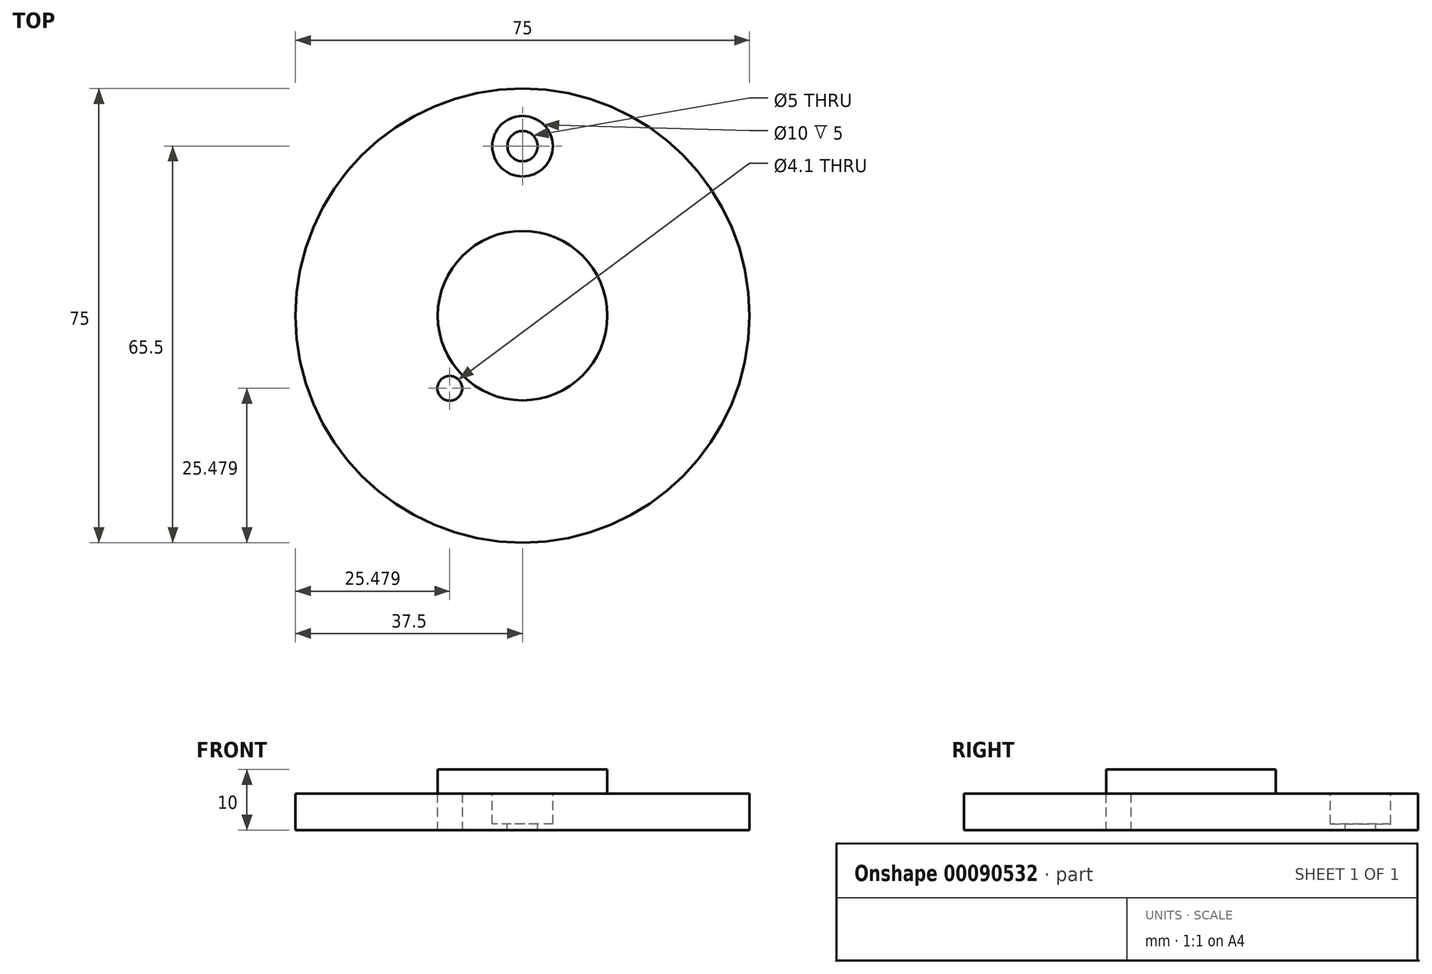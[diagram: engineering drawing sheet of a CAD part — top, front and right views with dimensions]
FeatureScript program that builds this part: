
annotation { "Feature Type Name" : "Feature", "Feature Type Description" : "" }
export const myFeature = defineFeature(function(context is Context, id is Id, definition is map)
    precondition{}
    {
        {
            var Q0;
            Q0=qCreatedBy(makeId("Top.planeOp"),FACE);
            var sketch = newSketch(context, id + "F0", { "sketchPlane" : qUnion([Q0])});
            skCircle(sketch, "E0", {"center": v(0, 0) * mm, "radius": 37.5 * mm});
            skSolve(sketch);
        }
        {
            var Q0;
            Q0=makeQuery(id+"F0.imprint","IMPRINT",FACE,{"disambiguationData":[TD([[makeQuery(id+"F0.imprint","IMPRINT",EDGE,{"derivedFrom":sQuery(id+"F0.wireOp",EDGE,"E0")}),1.0]])]});
            extrude(context, id + "F1", {"entities" : qUnion([Q0]), "depth" : 10 * mm});
        }
        {
            var Q0;
            Q0=makeQuery(id+"F1.opExtrude","CAP_FACE",FACE,{"disambiguationData":[OSD([sQuery(id+"F0.wireOp",EDGE,"E0")])],"isStart":false});
            var sketch = newSketch(context, id + "F2", { "sketchPlane" : qUnion([Q0])});
            skCircle(sketch, "E1", {"center": v(0, 0) * mm, "radius": 14 * mm});
            skSolve(sketch);
        }
        {
            var Q0;
            Q0=makeQuery(id+"F2.imprint","IMPRINT",FACE,{"disambiguationData":[TD([[makeQuery(id+"F2.imprint","IMPRINT",EDGE,{"derivedFrom":sQuery(id+"F2.wireOp",EDGE,"E1")}),-1.0]])]});
            extrude(context, id + "F3", {"entities" : qUnion([Q0]), "operationType" : NewBodyOperationType.REMOVE, "oppositeDirection" : true, "depth" : 4 * mm});
        }
        {
            var Q0;
            Q0=makeQuery(id+"F3.boolean.opBoolean","COPY",FACE,{"derivedFrom":makeQuery(id+"F3.opExtrude","CAP_FACE",FACE,{"disambiguationData":[OSD([sQuery(id+"F0.wireOp",EDGE,"E0"),sQuery(id+"F2.wireOp",EDGE,"E1")])],"isStart":false})});
            var sketch = newSketch(context, id + "F4", { "sketchPlane" : qUnion([Q0])});
            skCircle(sketch, "E2", {"center": v(0, 0) * mm, "radius": 28 * mm, "construction": true});
            skPoint(sketch, "E3", {"position": v(0, 28) * mm});
            skSolve(sketch);
        }
        {
            var Q0;
            Q0=sQuery(id+"F4.wireOp",VERTEX,"E3");
            var Q1;
            Q1=sQuery(id+"F4.wireOp",VERTEX,"5a48b65d-17f8-4e40-85f7-70837d0b4d29.1.0");
            var Q2;
            Q2=sQuery(id+"F4.wireOp",VERTEX,"5a48b65d-17f8-4e40-85f7-70837d0b4d29.2.0");
            var Q3;
            Q3=sQuery(id+"F4.wireOp",VERTEX,"5a48b65d-17f8-4e40-85f7-70837d0b4d29.3.0");
            var Q4;
            Q4=makeQuery(id+"F1.opExtrude","SWEPT_BODY",BODY,{"disambiguationData":[OSD([sQuery(id+"F0.wireOp",EDGE,"E0")])]});
            hole(context, id + "F5", {"style" : HoleStyle.C_BORE, "endStyle" : HoleEndStyle.THROUGH, "holeDiameter" : 5 * mm, "cBoreDiameter" : 10 * mm, "cBoreDepth" : 5 * mm, "startFromSketch" : true, "locations" : qUnion([Q0, Q1, Q2, Q3]), "scope" : qUnion([Q4]), "isTappedThrough" : true});
        }
        {
            var Q0;
            Q0=makeQuery(id+"F0.imprint","IMPRINT",FACE,{"disambiguationData":[TD([[makeQuery(id+"F0.imprint","IMPRINT",EDGE,{"derivedFrom":sQuery(id+"F0.wireOp",EDGE,"E0")}),1.0]])]});
            var sketch = newSketch(context, id + "F6", { "sketchPlane" : qUnion([Q0])});
            skCircle(sketch, "E4", {"center": v(0, 0) * mm, "radius": 17 * mm, "construction": true});
            skPoint(sketch, "E5", {"position": v(-12.02, -12.02) * mm});
            skLineSegment(sketch, "E6", {"start": v(0, 0) * mm, "end": v(-12.02, -12.02) * mm, "construction": true});
            skSolve(sketch);
        }
        {
            var Q0;
            Q0=sQuery(id+"F6.wireOp",VERTEX,"E5");
            var Q1;
            Q1=makeQuery(id+"F1.opExtrude","SWEPT_BODY",BODY,{"disambiguationData":[OSD([sQuery(id+"F0.wireOp",EDGE,"E0")])]});
            hole(context, id + "F7", {"style" : HoleStyle.SIMPLE, "endStyle" : HoleEndStyle.THROUGH, "oppositeDirection" : true, "standardTappedOrClearance" : lookupTablePath({ "standard" : "ISO", "engagement" : "75%", "pitch" : "0.9 mm", "size" : "M5", "type" : "Tapped" }), "standardBlindInLast" : lookupTablePath({ "standard" : "ISO", "engagement" : "75%", "pitch" : "0.9 mm", "size" : "M5", "type" : "Tapped" }), "holeDiameter" : 4.1 * mm, "startFromSketch" : true, "locations" : qUnion([Q0]), "scope" : qUnion([Q1]), "isTappedThrough" : true, "showTappedDepth" : true});
        }
    });
